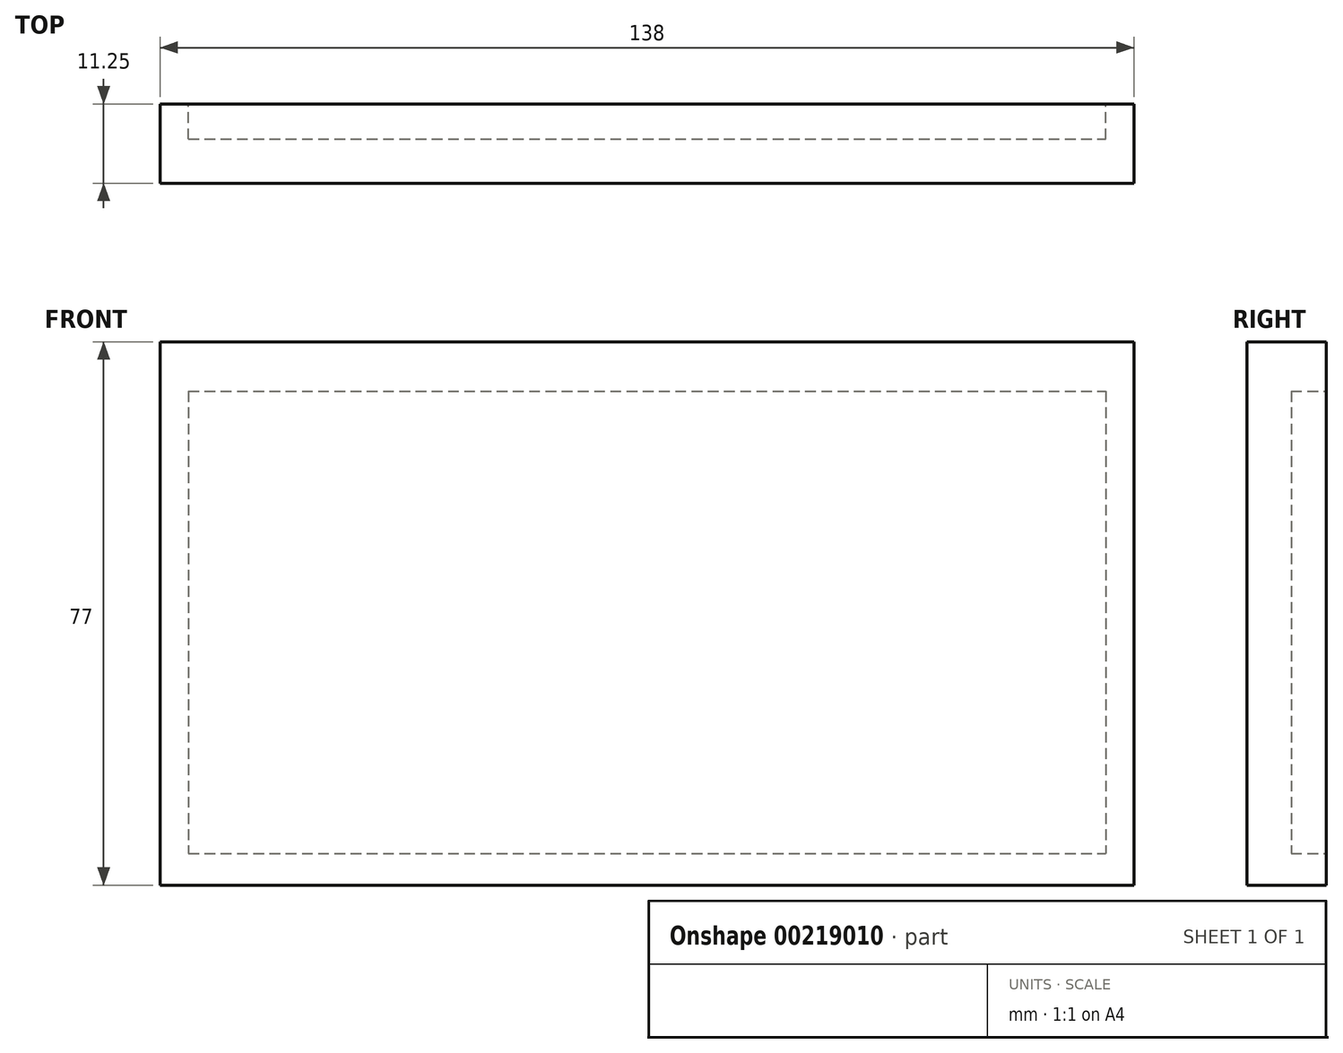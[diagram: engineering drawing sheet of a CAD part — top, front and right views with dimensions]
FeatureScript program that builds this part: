
annotation { "Feature Type Name" : "Feature", "Feature Type Description" : "" }
export const myFeature = defineFeature(function(context is Context, id is Id, definition is map)
    precondition{}
    {
        {
            var Q0;
            Q0=qCreatedBy(makeId("Front.planeOp"),FACE);
            var sketch = newSketch(context, id + "F0", { "sketchPlane" : qUnion([Q0])});
            skLineSegment(sketch, "E0.bottom", {"start": v(0, 0) * mm, "end": v(138, 0) * mm});
            skLineSegment(sketch, "E0.top", {"start": v(0, 77) * mm, "end": v(138, 77) * mm});
            skLineSegment(sketch, "E0.left", {"start": v(0, 0) * mm, "end": v(0, 77) * mm});
            skLineSegment(sketch, "E0.right", {"start": v(138, 0) * mm, "end": v(138, 77) * mm});
            skSolve(sketch);
        }
        {
            var Q0;
            Q0=makeQuery(id+"F0.imprint","IMPRINT",FACE,{"disambiguationData":[TD([[makeQuery(id+"F0.imprint","IMPRINT",EDGE,{"derivedFrom":sQuery(id+"F0.wireOp",EDGE,"E0.bottom")}),1.0]])]});
            extrude(context, id + "F1", {"entities" : qUnion([Q0]), "depth" : 11.25 * mm});
        }
        {
            var Q0;
            Q0=qCreatedBy(makeId("Front.planeOp"),FACE);
            var sketch = newSketch(context, id + "F2", { "sketchPlane" : qUnion([Q0])});
            skLineSegment(sketch, "E1.bottom", {"start": v(4, 70) * mm, "end": v(134, 70) * mm});
            skLineSegment(sketch, "E1.top", {"start": v(4, 4.5) * mm, "end": v(134, 4.5) * mm});
            skLineSegment(sketch, "E1.left", {"start": v(4, 70) * mm, "end": v(4, 4.5) * mm});
            skLineSegment(sketch, "E1.right", {"start": v(134, 70) * mm, "end": v(134, 4.5) * mm});
            skSolve(sketch);
        }
        {
            var Q0;
            Q0 = qSketchRegion(id + "F2", true);
            extrude(context, id + "F3", {"entities" : qUnion([Q0]), "operationType" : NewBodyOperationType.REMOVE, "depth" : 5 * mm});
        }
    });
